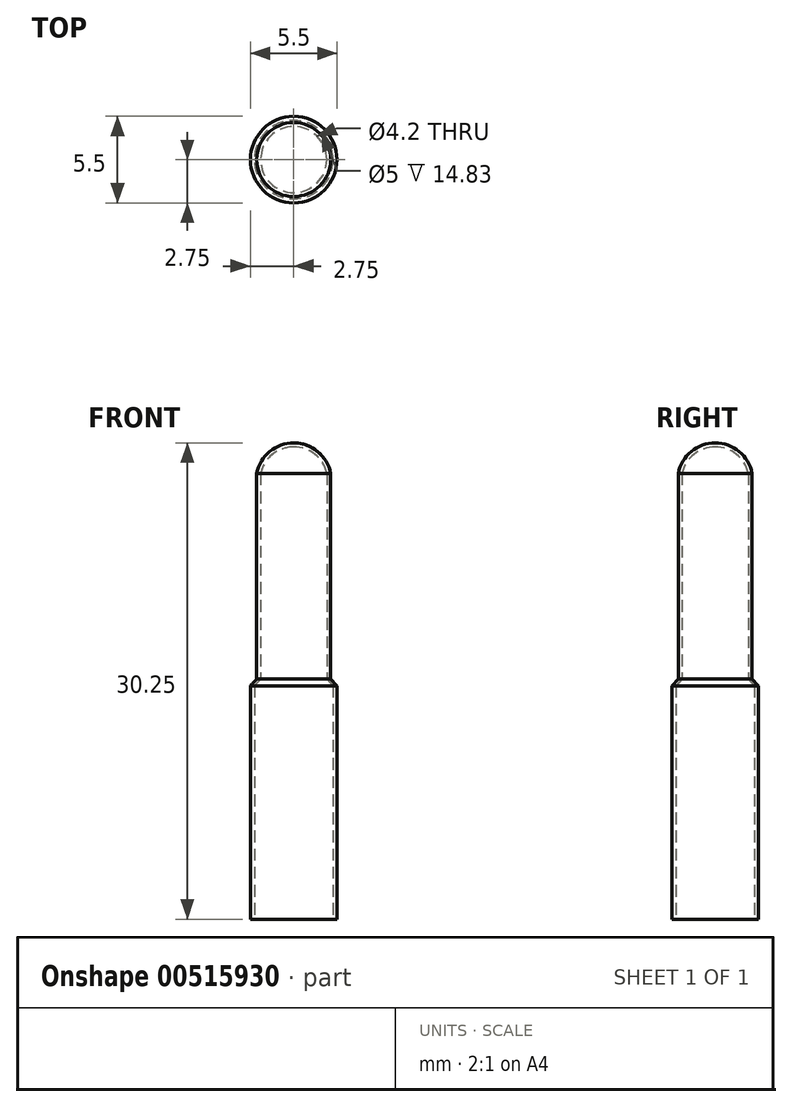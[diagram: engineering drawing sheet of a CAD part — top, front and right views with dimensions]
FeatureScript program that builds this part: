
annotation { "Feature Type Name" : "Feature", "Feature Type Description" : "" }
export const myFeature = defineFeature(function(context is Context, id is Id, definition is map)
    precondition{}
    {
        {
            var Q0;
            Q0=qCreatedBy(makeId("Front.planeOp"),FACE);
            var sketch = newSketch(context, id + "F0", { "sketchPlane" : qUnion([Q0])});
            skLineSegment(sketch, "E0", {"start": v(-2.5, 0) * mm, "end": v(-2.5, 14.83) * mm});
            skLineSegment(sketch, "E1", {"start": v(-2.75, 0) * mm, "end": v(-2.75, 14.83) * mm});
            skLineSegment(sketch, "E2", {"start": v(-2.1, 15.25) * mm, "end": v(-2.1, 28.32) * mm});
            skLineSegment(sketch, "E3", {"start": v(-2.35, 15.67) * mm, "end": v(-2.35, 28.32) * mm});
            skArc(sketch, "E4", {"start": v(-2.35, 28.32) * mm, "mid": v(-1.52, 29.7) * mm, "end": v(0, 30.25) * mm});
            skArc(sketch, "E5", {"start": v(-2.1, 28.32) * mm, "mid": v(-1.35, 29.53) * mm, "end": v(0, 30) * mm});
            skLineSegment(sketch, "E6", {"start": v(0, 30.25) * mm, "end": v(0, 15.25) * mm});
            skLineSegment(sketch, "E7", {"start": v(0, 0) * mm, "end": v(0, 30.25) * mm});
            skLineSegment(sketch, "E8", {"start": v(-2.75, 0) * mm, "end": v(-2.5, 0) * mm});
            skLineSegment(sketch, "E9", {"start": v(-2.1, 15.25) * mm, "end": v(-2.1, 14.83) * mm});
            skLineSegment(sketch, "E10", {"start": v(-2.1, 15.25) * mm, "end": v(-2.5, 14.83) * mm});
            skLineSegment(sketch, "E11", {"start": v(-2.35, 15.25) * mm, "end": v(-2.75, 14.83) * mm});
            skLineSegment(sketch, "E12", {"start": v(-2.35, 15.25) * mm, "end": v(-2.35, 15.67) * mm});
            skSolve(sketch);
        }
        {
            var Q0;
            Q0=makeQuery(id+"F0.imprint","IMPRINT",FACE,{"disambiguationData":[TD([[makeQuery(id+"F0.imprint","IMPRINT",EDGE,{"derivedFrom":sQuery(id+"F0.wireOp",EDGE,"E0")}),1.0]])]});
            var Q1;
            Q1=sQuery(id+"F0.wireOp",EDGE,"E7");
            revolve(context, id + "F1", {"entities" : qUnion([Q0]), "axis" : qUnion([Q1]), "revolveType" : RevolveType.FULL});
        }
    });
